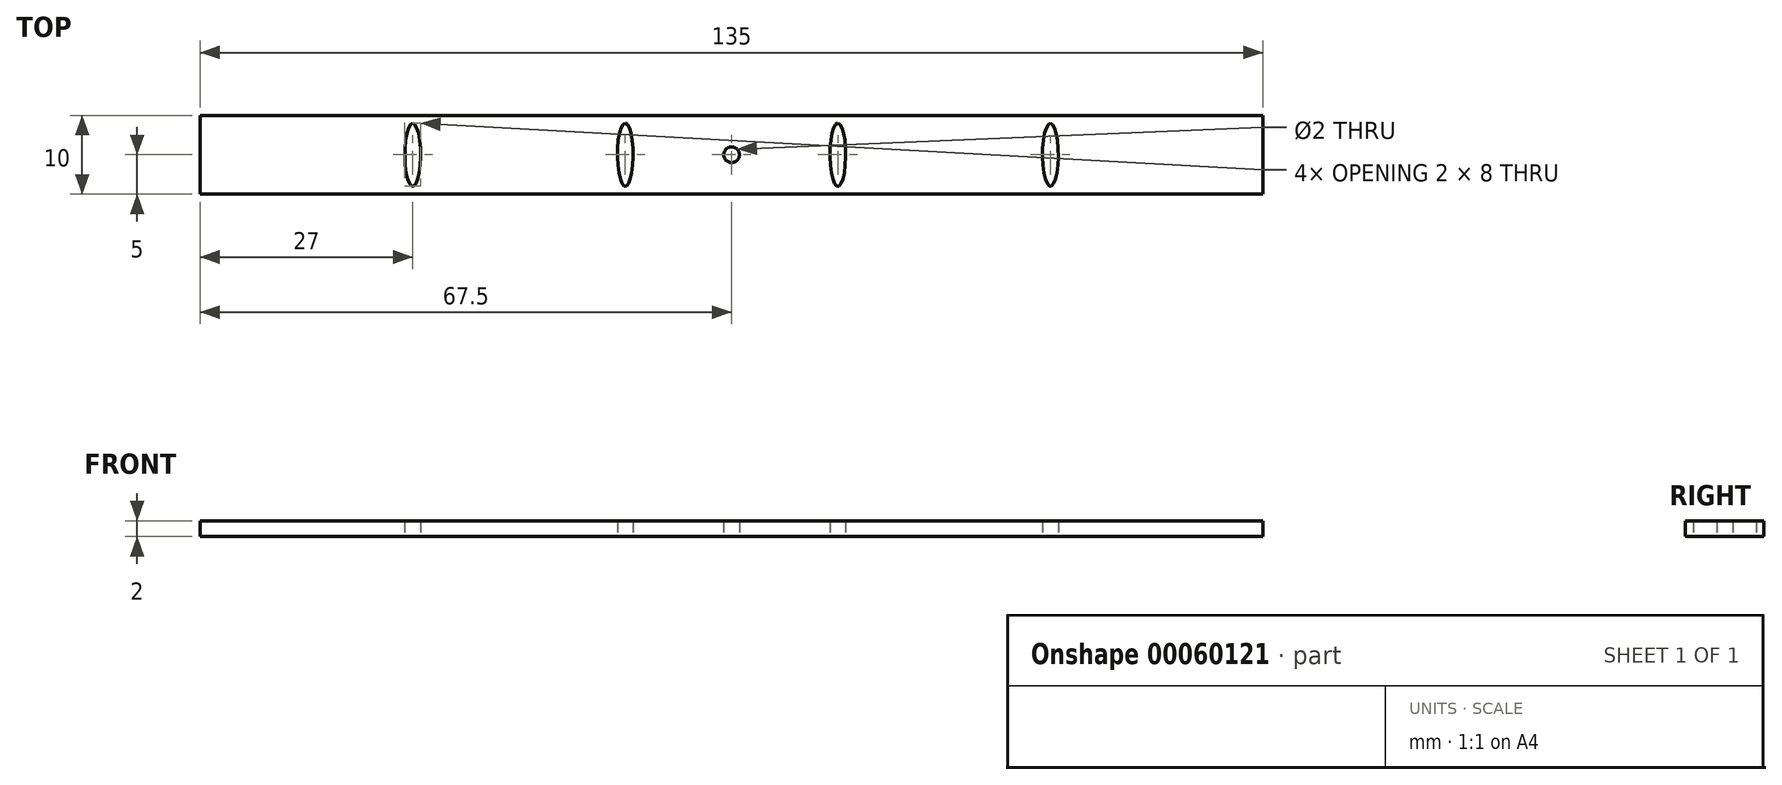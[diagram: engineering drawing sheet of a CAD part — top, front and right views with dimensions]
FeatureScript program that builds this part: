
annotation { "Feature Type Name" : "Feature", "Feature Type Description" : "" }
export const myFeature = defineFeature(function(context is Context, id is Id, definition is map)
    precondition{}
    {
        {
            var Q0;
            Q0=qCreatedBy(makeId("Top.planeOp"),FACE);
            var sketch = newSketch(context, id + "F0", { "sketchPlane" : qUnion([Q0])});
            skLineSegment(sketch, "E0.bottom", {"start": v(67.5, -5) * mm, "end": v(-67.5, -5) * mm});
            skLineSegment(sketch, "E0.top", {"start": v(67.5, 5) * mm, "end": v(-67.5, 5) * mm});
            skLineSegment(sketch, "E0.left", {"start": v(67.5, -5) * mm, "end": v(67.5, 5) * mm});
            skLineSegment(sketch, "E0.right", {"start": v(-67.5, -5) * mm, "end": v(-67.5, 5) * mm});
            skPoint(sketch, "E0.middle", {"position": v(0, 0) * mm});
            skCircle(sketch, "E1", {"center": v(0, 0) * mm, "radius": 1 * mm});
            skLineSegment(sketch, "E2", {"start": v(0, 0) * mm, "end": v(13.5, 0) * mm, "construction": true});
            skLineSegment(sketch, "E3", {"start": v(13.5, 0) * mm, "end": v(40.5, 0) * mm, "construction": true});
            skPoint(sketch, "E3.endSnap0", {"position": v(67.5, 0) * mm});
            skLineSegment(sketch, "E4", {"start": v(40.5, 0) * mm, "end": v(67.5, 0) * mm, "construction": true});
            skLineSegment(sketch, "E5", {"start": v(13.5, 5) * mm, "end": v(13.5, -5) * mm, "construction": true});
            skLineSegment(sketch, "E6", {"start": v(40.5, 5) * mm, "end": v(40.5, -5) * mm, "construction": true});
            skEllipse(sketch, "E7", {"center": v(13.5, 0) * mm, "majorRadius": 4 * mm, "minorRadius": 1 * mm, "majorAxis": v(0, 1)});
            skEllipse(sketch, "E8", {"center": v(40.5, 0) * mm, "majorRadius": 4 * mm, "minorRadius": 1 * mm, "majorAxis": v(0, 1)});
            skEllipse(sketch, "E9.MirrorC", {"center": v(-13.5, 0) * mm, "majorRadius": 4 * mm, "minorRadius": 1 * mm, "majorAxis": v(0, 1)});
            skEllipse(sketch, "E10.MirrorC", {"center": v(-40.5, 0) * mm, "majorRadius": 4 * mm, "minorRadius": 1 * mm, "majorAxis": v(0, 1)});
            skSolve(sketch);
        }
        {
            var Q0;
            Q0=makeQuery(id+"F0.imprint","IMPRINT",FACE,{"disambiguationData":[TD([[makeQuery(id+"F0.imprint","IMPRINT",EDGE,{"derivedFrom":sQuery(id+"F0.wireOp",EDGE,"E0.bottom")}),-1.0]])]});
            extrude(context, id + "F1", {"entities" : qUnion([Q0]), "depth" : 2 * mm});
        }
    });
